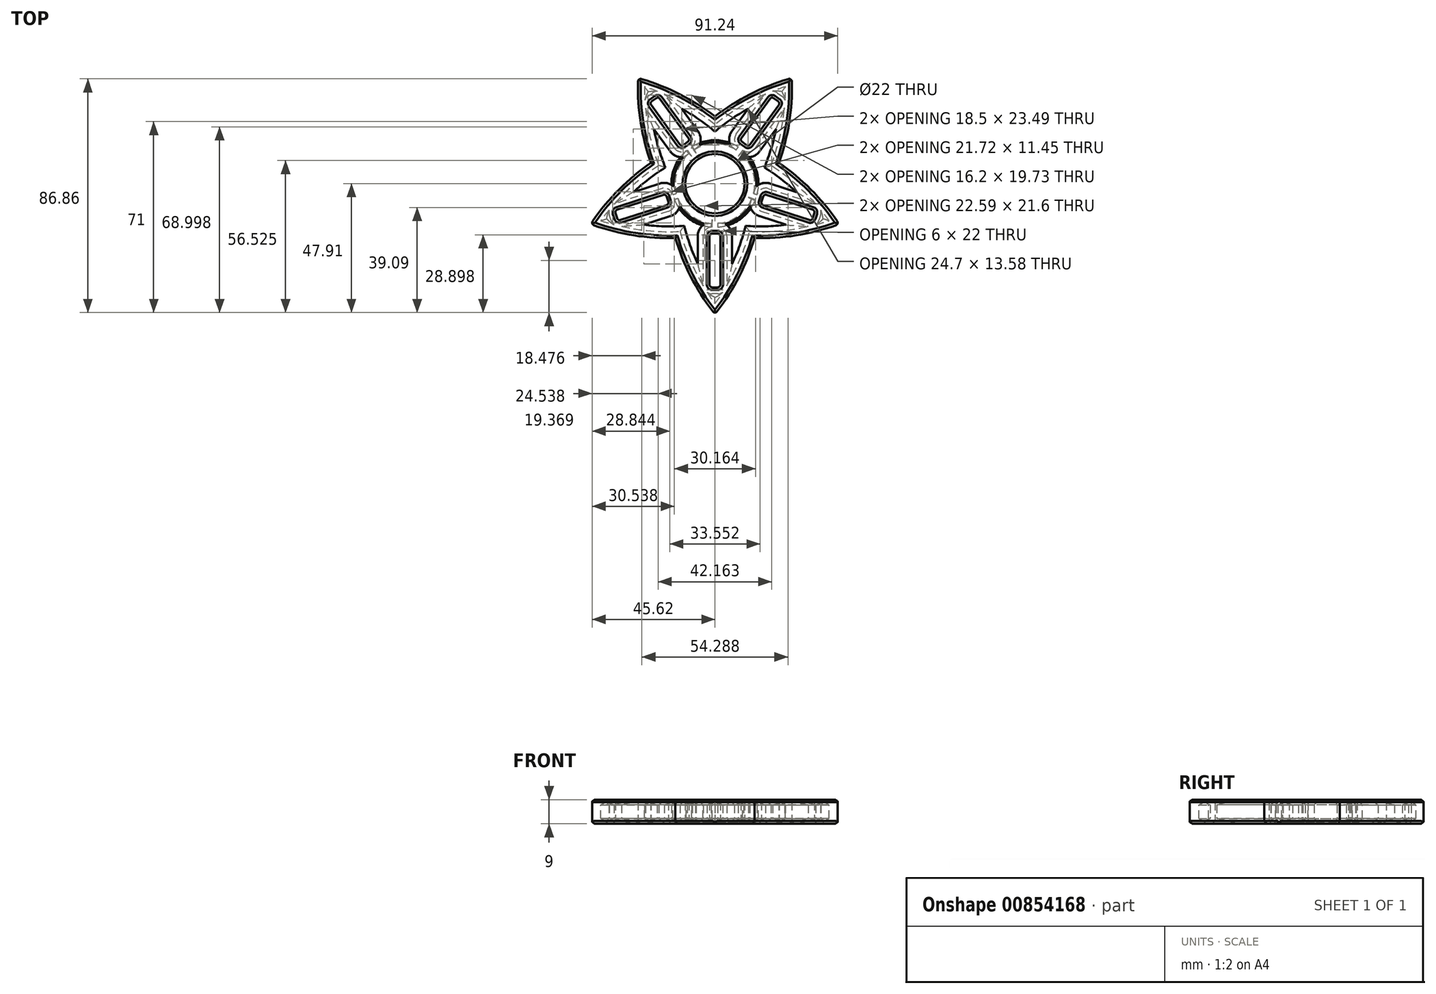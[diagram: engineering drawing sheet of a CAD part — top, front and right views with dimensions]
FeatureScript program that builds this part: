
annotation { "Feature Type Name" : "Feature", "Feature Type Description" : "" }
export const myFeature = defineFeature(function(context is Context, id is Id, definition is map)
    precondition{}
    {
        {
            var Q0;
            Q0=qCreatedBy(makeId("Top.planeOp"),FACE);
            var sketch = newSketch(context, id + "F0", { "sketchPlane" : qUnion([Q0])});
            skCircle(sketch, "E0", {"center": v(0, 0) * mm, "radius": 11 * mm});
            skCircle(sketch, "E1", {"center": v(0, 0) * mm, "radius": 15 * mm});
            skLineSegment(sketch, "E2.0", {"start": v(-10.9, 15) * mm, "end": v(10.9, 15) * mm});
            skLineSegment(sketch, "E2.1", {"start": v(10.9, 15) * mm, "end": v(17.63, -5.73) * mm});
            skLineSegment(sketch, "E2.2", {"start": v(17.63, -5.73) * mm, "end": v(0, -18.54) * mm});
            skLineSegment(sketch, "E2.3", {"start": v(0, -18.54) * mm, "end": v(-17.63, -5.73) * mm});
            skLineSegment(sketch, "E2.4", {"start": v(-17.63, -5.73) * mm, "end": v(-10.9, 15) * mm});
            skPoint(sketch, "E2.0.midPoint", {"position": v(0, 15) * mm});
            skLineSegment(sketch, "E3", {"start": v(-10.9, 15) * mm, "end": v(-28.53, 39.27) * mm});
            skLineSegment(sketch, "E4", {"start": v(-17.63, -5.73) * mm, "end": v(-46.17, -15) * mm});
            skLineSegment(sketch, "E5", {"start": v(0, -18.54) * mm, "end": v(0, -48.54) * mm});
            skLineSegment(sketch, "E6", {"start": v(17.63, -5.73) * mm, "end": v(46.17, -15) * mm});
            skLineSegment(sketch, "E7", {"start": v(10.9, 15) * mm, "end": v(28.53, 39.27) * mm});
            skLineSegment(sketch, "E8", {"start": v(14.27, 4.64) * mm, "end": v(23.78, 7.73) * mm});
            skLineSegment(sketch, "E9", {"start": v(0, 15) * mm, "end": v(0, 25) * mm});
            skLineSegment(sketch, "E10", {"start": v(-8.82, -12.14) * mm, "end": v(-14.7, -20.23) * mm});
            skLineSegment(sketch, "E11", {"start": v(8.82, -12.14) * mm, "end": v(14.7, -20.23) * mm});
            skLineSegment(sketch, "E12", {"start": v(-14.27, 4.64) * mm, "end": v(-23.78, 7.73) * mm});
            skArc(sketch, "E13", {"start": v(28.53, 39.27) * mm, "mid": v(7.11, 29.9) * mm, "end": v(-10.9, 15) * mm});
            skArc(sketch, "E14", {"start": v(-28.53, 39.27) * mm, "mid": v(-26.24, 16) * mm, "end": v(-17.63, -5.73) * mm});
            skArc(sketch, "E15", {"start": v(10.9, 15) * mm, "mid": v(-7.11, 29.9) * mm, "end": v(-28.53, 39.27) * mm});
            skArc(sketch, "E16", {"start": v(-10.9, 15) * mm, "mid": v(-30.64, 2.47) * mm, "end": v(-46.17, -15) * mm});
            skArc(sketch, "E17", {"start": v(-46.17, -15) * mm, "mid": v(-23.33, -20) * mm, "end": v(0, -18.54) * mm});
            skArc(sketch, "E18", {"start": v(-17.63, -5.73) * mm, "mid": v(-11.82, -28.37) * mm, "end": v(0, -48.54) * mm});
            skArc(sketch, "E19", {"start": v(0, -18.54) * mm, "mid": v(23.33, -20) * mm, "end": v(46.17, -15) * mm});
            skArc(sketch, "E20", {"start": v(0, -48.54) * mm, "mid": v(11.82, -28.37) * mm, "end": v(17.63, -5.73) * mm});
            skArc(sketch, "E21", {"start": v(17.63, -5.73) * mm, "mid": v(26.24, 16) * mm, "end": v(28.53, 39.27) * mm});
            skArc(sketch, "E22", {"start": v(46.17, -15) * mm, "mid": v(30.64, 2.47) * mm, "end": v(10.9, 15) * mm});
            skLineSegment(sketch, "E23", {"start": v(0, -18.54) * mm, "end": v(0, -33.54) * mm});
            skLineSegment(sketch, "E24.bottom", {"start": v(-1, -38.54) * mm, "end": v(1, -38.54) * mm});
            skLineSegment(sketch, "E24.top", {"start": v(-1, -18.54) * mm, "end": v(1, -18.54) * mm});
            skLineSegment(sketch, "E24.left", {"start": v(-2, -37.54) * mm, "end": v(-2, -19.54) * mm});
            skLineSegment(sketch, "E24.right", {"start": v(2, -37.54) * mm, "end": v(2, -19.54) * mm});
            skPoint(sketch, "E24.middle", {"position": v(0, -28.54) * mm});
            skPoint(sketch, "E25.visualSharp", {"position": v(-2, -18.54) * mm});
            skArc(sketch, "E25.filletArc", {"start": v(-1, -18.54) * mm, "mid": v(-1.7, -18.83) * mm, "end": v(-2, -19.54) * mm});
            skPoint(sketch, "E26.visualSharp", {"position": v(2, -18.54) * mm});
            skArc(sketch, "E26.filletArc", {"start": v(2, -19.54) * mm, "mid": v(1.7, -18.83) * mm, "end": v(1, -18.54) * mm});
            skPoint(sketch, "E27.visualSharp", {"position": v(-2, -38.54) * mm});
            skArc(sketch, "E27.filletArc", {"start": v(-2, -37.54) * mm, "mid": v(-1.7, -38.25) * mm, "end": v(-1, -38.54) * mm});
            skPoint(sketch, "E28.visualSharp", {"position": v(2, -38.54) * mm});
            skArc(sketch, "E28.filletArc", {"start": v(1, -38.54) * mm, "mid": v(1.7, -38.25) * mm, "end": v(2, -37.54) * mm});
            skLineSegment(sketch, "E29.1.0", {"start": v(35.09, -13.5) * mm, "end": v(17.97, -7.94) * mm});
            skPoint(sketch, "E29.1.1", {"position": v(18.25, -3.83) * mm});
            skPoint(sketch, "E29.1.2", {"position": v(36.04, -13.81) * mm});
            skLineSegment(sketch, "E29.1.3", {"start": v(36.32, -9.7) * mm, "end": v(19.2, -4.14) * mm});
            skPoint(sketch, "E29.1.4", {"position": v(17.02, -7.63) * mm});
            skPoint(sketch, "E29.1.5", {"position": v(37.27, -10) * mm});
            skLineSegment(sketch, "E29.1.6", {"start": v(17.63, -5.73) * mm, "end": v(31.9, -10.36) * mm});
            skArc(sketch, "E29.1.7", {"start": v(35.09, -13.5) * mm, "mid": v(35.85, -13.44) * mm, "end": v(36.35, -12.86) * mm});
            skArc(sketch, "E29.1.8", {"start": v(17.32, -6.68) * mm, "mid": v(17.38, -7.44) * mm, "end": v(17.97, -7.94) * mm});
            skArc(sketch, "E29.1.9", {"start": v(19.2, -4.14) * mm, "mid": v(18.44, -4.2) * mm, "end": v(17.94, -4.78) * mm});
            skArc(sketch, "E29.1.10", {"start": v(36.96, -10.96) * mm, "mid": v(36.9, -10.2) * mm, "end": v(36.32, -9.7) * mm});
            skLineSegment(sketch, "E29.1.11", {"start": v(36.35, -12.86) * mm, "end": v(36.96, -10.96) * mm});
            skLineSegment(sketch, "E29.1.12", {"start": v(17.32, -6.68) * mm, "end": v(17.94, -4.78) * mm});
            skPoint(sketch, "E29.1.13", {"position": v(27.14, -8.82) * mm});
            skLineSegment(sketch, "E29.2.0", {"start": v(23.68, 29.2) * mm, "end": v(13.1, 14.63) * mm});
            skPoint(sketch, "E29.2.1", {"position": v(9.28, 16.18) * mm});
            skPoint(sketch, "E29.2.2", {"position": v(24.27, 30) * mm});
            skLineSegment(sketch, "E29.2.3", {"start": v(20.45, 31.55) * mm, "end": v(9.87, 16.98) * mm});
            skPoint(sketch, "E29.2.4", {"position": v(12.52, 13.82) * mm});
            skPoint(sketch, "E29.2.5", {"position": v(21.04, 32.36) * mm});
            skLineSegment(sketch, "E29.2.6", {"start": v(10.9, 15) * mm, "end": v(19.71, 27.14) * mm});
            skArc(sketch, "E29.2.7", {"start": v(23.68, 29.2) * mm, "mid": v(23.86, 29.94) * mm, "end": v(23.46, 30.6) * mm});
            skArc(sketch, "E29.2.8", {"start": v(11.7, 14.41) * mm, "mid": v(12.45, 14.23) * mm, "end": v(13.1, 14.63) * mm});
            skArc(sketch, "E29.2.9", {"start": v(9.87, 16.98) * mm, "mid": v(9.69, 16.24) * mm, "end": v(10.09, 15.59) * mm});
            skArc(sketch, "E29.2.10", {"start": v(21.84, 31.77) * mm, "mid": v(21.1, 31.95) * mm, "end": v(20.45, 31.55) * mm});
            skLineSegment(sketch, "E29.2.11", {"start": v(23.46, 30.6) * mm, "end": v(21.84, 31.77) * mm});
            skLineSegment(sketch, "E29.2.12", {"start": v(11.7, 14.41) * mm, "end": v(10.09, 15.59) * mm});
            skPoint(sketch, "E29.2.13", {"position": v(16.78, 23.1) * mm});
            skLineSegment(sketch, "E29.3.0", {"start": v(-20.45, 31.55) * mm, "end": v(-9.87, 16.98) * mm});
            skPoint(sketch, "E29.3.1", {"position": v(-12.52, 13.82) * mm});
            skPoint(sketch, "E29.3.2", {"position": v(-21.04, 32.36) * mm});
            skLineSegment(sketch, "E29.3.3", {"start": v(-23.68, 29.2) * mm, "end": v(-13.1, 14.63) * mm});
            skPoint(sketch, "E29.3.4", {"position": v(-9.28, 16.18) * mm});
            skPoint(sketch, "E29.3.5", {"position": v(-24.27, 30) * mm});
            skLineSegment(sketch, "E29.3.6", {"start": v(-10.9, 15) * mm, "end": v(-19.71, 27.14) * mm});
            skArc(sketch, "E29.3.7", {"start": v(-20.45, 31.55) * mm, "mid": v(-21.1, 31.95) * mm, "end": v(-21.84, 31.77) * mm});
            skArc(sketch, "E29.3.8", {"start": v(-10.09, 15.59) * mm, "mid": v(-9.69, 16.24) * mm, "end": v(-9.87, 16.98) * mm});
            skArc(sketch, "E29.3.9", {"start": v(-13.1, 14.63) * mm, "mid": v(-12.45, 14.23) * mm, "end": v(-11.7, 14.41) * mm});
            skArc(sketch, "E29.3.10", {"start": v(-23.46, 30.6) * mm, "mid": v(-23.86, 29.94) * mm, "end": v(-23.68, 29.2) * mm});
            skLineSegment(sketch, "E29.3.11", {"start": v(-21.84, 31.77) * mm, "end": v(-23.46, 30.6) * mm});
            skLineSegment(sketch, "E29.3.12", {"start": v(-10.09, 15.59) * mm, "end": v(-11.7, 14.41) * mm});
            skPoint(sketch, "E29.3.13", {"position": v(-16.78, 23.1) * mm});
            skLineSegment(sketch, "E29.4.0", {"start": v(-36.32, -9.7) * mm, "end": v(-19.2, -4.14) * mm});
            skPoint(sketch, "E29.4.1", {"position": v(-17.02, -7.63) * mm});
            skPoint(sketch, "E29.4.2", {"position": v(-37.27, -10) * mm});
            skLineSegment(sketch, "E29.4.3", {"start": v(-35.09, -13.5) * mm, "end": v(-17.97, -7.94) * mm});
            skPoint(sketch, "E29.4.4", {"position": v(-18.25, -3.83) * mm});
            skPoint(sketch, "E29.4.5", {"position": v(-36.04, -13.81) * mm});
            skLineSegment(sketch, "E29.4.6", {"start": v(-17.63, -5.73) * mm, "end": v(-31.9, -10.36) * mm});
            skArc(sketch, "E29.4.7", {"start": v(-36.32, -9.7) * mm, "mid": v(-36.9, -10.2) * mm, "end": v(-36.96, -10.96) * mm});
            skArc(sketch, "E29.4.8", {"start": v(-17.94, -4.78) * mm, "mid": v(-18.44, -4.2) * mm, "end": v(-19.2, -4.14) * mm});
            skArc(sketch, "E29.4.9", {"start": v(-17.97, -7.94) * mm, "mid": v(-17.38, -7.44) * mm, "end": v(-17.32, -6.68) * mm});
            skArc(sketch, "E29.4.10", {"start": v(-36.35, -12.86) * mm, "mid": v(-35.85, -13.44) * mm, "end": v(-35.09, -13.5) * mm});
            skLineSegment(sketch, "E29.4.11", {"start": v(-36.96, -10.96) * mm, "end": v(-36.35, -12.86) * mm});
            skLineSegment(sketch, "E29.4.12", {"start": v(-17.94, -4.78) * mm, "end": v(-17.32, -6.68) * mm});
            skPoint(sketch, "E29.4.13", {"position": v(-27.14, -8.82) * mm});
            skSolve(sketch);
        }
        {
            var Q0;
            {var subQ3=sQuery(id+"F0.wireOp",EDGE,"E9");Q0=makeQuery(id+"F0.imprint","IMPRINT",FACE,{"disambiguationData":[TD([[makeQuery(id+"F0.imprint","IMPRINT",EDGE,{"derivedFrom":subQ3}),1.0]])]});}
            var Q1;
            {var subQ3=sQuery(id+"F0.wireOp",EDGE,"E9");Q1=makeQuery(id+"F0.imprint","IMPRINT",FACE,{"disambiguationData":[TD([[makeQuery(id+"F0.imprint","IMPRINT",EDGE,{"derivedFrom":subQ3}),-1.0]])]});}
            var Q2;
            {var subQ3=sQuery(id+"F0.wireOp",EDGE,"E8");Q2=makeQuery(id+"F0.imprint","IMPRINT",FACE,{"disambiguationData":[TD([[makeQuery(id+"F0.imprint","IMPRINT",EDGE,{"derivedFrom":subQ3}),1.0]])]});}
            var Q3;
            {var subQ3=sQuery(id+"F0.wireOp",EDGE,"E8");Q3=makeQuery(id+"F0.imprint","IMPRINT",FACE,{"disambiguationData":[TD([[makeQuery(id+"F0.imprint","IMPRINT",EDGE,{"derivedFrom":subQ3}),-1.0]])]});}
            var Q4;
            {var subQ3=sQuery(id+"F0.wireOp",EDGE,"E11");Q4=makeQuery(id+"F0.imprint","IMPRINT",FACE,{"disambiguationData":[TD([[makeQuery(id+"F0.imprint","IMPRINT",EDGE,{"derivedFrom":subQ3}),1.0]])]});}
            var Q5;
            {var subQ3=sQuery(id+"F0.wireOp",EDGE,"E11");Q5=makeQuery(id+"F0.imprint","IMPRINT",FACE,{"disambiguationData":[TD([[makeQuery(id+"F0.imprint","IMPRINT",EDGE,{"derivedFrom":subQ3}),-1.0]])]});}
            var Q6;
            {var subQ3=sQuery(id+"F0.wireOp",EDGE,"E10");Q6=makeQuery(id+"F0.imprint","IMPRINT",FACE,{"disambiguationData":[TD([[makeQuery(id+"F0.imprint","IMPRINT",EDGE,{"derivedFrom":subQ3}),1.0]])]});}
            var Q7;
            {var subQ3=sQuery(id+"F0.wireOp",EDGE,"E10");Q7=makeQuery(id+"F0.imprint","IMPRINT",FACE,{"disambiguationData":[TD([[makeQuery(id+"F0.imprint","IMPRINT",EDGE,{"derivedFrom":subQ3}),-1.0]])]});}
            var Q8;
            {var subQ3=sQuery(id+"F0.wireOp",EDGE,"E12");Q8=makeQuery(id+"F0.imprint","IMPRINT",FACE,{"disambiguationData":[TD([[makeQuery(id+"F0.imprint","IMPRINT",EDGE,{"derivedFrom":subQ3}),1.0]])]});}
            var Q9;
            {var subQ3=sQuery(id+"F0.wireOp",EDGE,"E12");Q9=makeQuery(id+"F0.imprint","IMPRINT",FACE,{"disambiguationData":[TD([[makeQuery(id+"F0.imprint","IMPRINT",EDGE,{"derivedFrom":subQ3}),-1.0]])]});}
            var Q10;
            Q10=makeQuery(id+"F0.imprint","IMPRINT",FACE,{"disambiguationData":[TD([[makeQuery(id+"F0.imprint","IMPRINT",EDGE,{"derivedFrom":sQuery(id+"F0.wireOp",EDGE,"03f61230-8e6a-4787-a5c0-0c1afcc67b7a.3.3")}),-1.0]])]});
            var Q11;
            Q11=makeQuery(id+"F0.imprint","IMPRINT",FACE,{"disambiguationData":[TD([[makeQuery(id+"F0.imprint","IMPRINT",EDGE,{"derivedFrom":sQuery(id+"F0.wireOp",EDGE,"03f61230-8e6a-4787-a5c0-0c1afcc67b7a.4.1")}),1.0]])]});
            var Q12;
            Q12=makeQuery(id+"F0.imprint","IMPRINT",FACE,{"disambiguationData":[TD([[makeQuery(id+"F0.imprint","IMPRINT",EDGE,{"derivedFrom":sQuery(id+"F0.wireOp",EDGE,"03f61230-8e6a-4787-a5c0-0c1afcc67b7a.4.3")}),-1.0]])]});
            var Q13;
            Q13=makeQuery(id+"F0.imprint","IMPRINT",FACE,{"disambiguationData":[TD([[makeQuery(id+"F0.imprint","IMPRINT",EDGE,{"derivedFrom":sQuery(id+"F0.wireOp",EDGE,"E24.left")}),1.0]])]});
            var Q14;
            Q14=makeQuery(id+"F0.imprint","IMPRINT",FACE,{"disambiguationData":[TD([[makeQuery(id+"F0.imprint","IMPRINT",EDGE,{"derivedFrom":sQuery(id+"F0.wireOp",EDGE,"E24.right")}),-1.0]])]});
            var Q15;
            Q15=makeQuery(id+"F0.imprint","IMPRINT",FACE,{"disambiguationData":[TD([[makeQuery(id+"F0.imprint","IMPRINT",EDGE,{"derivedFrom":sQuery(id+"F0.wireOp",EDGE,"03f61230-8e6a-4787-a5c0-0c1afcc67b7a.1.1")}),1.0]])]});
            var Q16;
            Q16=makeQuery(id+"F0.imprint","IMPRINT",FACE,{"disambiguationData":[TD([[makeQuery(id+"F0.imprint","IMPRINT",EDGE,{"derivedFrom":sQuery(id+"F0.wireOp",EDGE,"03f61230-8e6a-4787-a5c0-0c1afcc67b7a.1.3")}),-1.0]])]});
            var Q17;
            Q17=makeQuery(id+"F0.imprint","IMPRINT",FACE,{"disambiguationData":[TD([[makeQuery(id+"F0.imprint","IMPRINT",EDGE,{"derivedFrom":sQuery(id+"F0.wireOp",EDGE,"03f61230-8e6a-4787-a5c0-0c1afcc67b7a.2.3")}),-1.0]])]});
            var Q18;
            Q18=makeQuery(id+"F0.imprint","IMPRINT",FACE,{"disambiguationData":[TD([[makeQuery(id+"F0.imprint","IMPRINT",EDGE,{"derivedFrom":sQuery(id+"F0.wireOp",EDGE,"03f61230-8e6a-4787-a5c0-0c1afcc67b7a.2.1")}),1.0]])]});
            var Q19;
            Q19=makeQuery(id+"F0.imprint","IMPRINT",FACE,{"disambiguationData":[TD([[makeQuery(id+"F0.imprint","IMPRINT",EDGE,{"derivedFrom":sQuery(id+"F0.wireOp",EDGE,"03f61230-8e6a-4787-a5c0-0c1afcc67b7a.3.1")}),1.0]])]});
            var Q20;
            {var subQ0=sQuery(id+"F0.wireOp",EDGE,"E2.0");var subQ1=sQuery(id+"F0.wireOp",EDGE,"E1");var subQ2=makeQuery(id+"F0.imprint","INTERSECT",VERTEX,{"derivedFrom":[subQ1,subQ0,sQuery(id+"F0.wireOp",EDGE,"E9")]});Q20=makeQuery(id+"F0.imprint","IMPRINT",FACE,{"disambiguationData":[TD([[makeQuery(id+"F0.imprint","IMPRINT",EDGE,{"disambiguationData":[TD([[subQ2,-1.0]])],"derivedFrom":subQ1}),-1.0]])]});}
            var Q21;
            {var subQ0=sQuery(id+"F0.wireOp",EDGE,"E2.3");var subQ1=sQuery(id+"F0.wireOp",EDGE,"E1");var subQ2=makeQuery(id+"F0.imprint","INTERSECT",VERTEX,{"derivedFrom":[subQ1,subQ0,sQuery(id+"F0.wireOp",EDGE,"E10")]});Q21=makeQuery(id+"F0.imprint","IMPRINT",FACE,{"disambiguationData":[TD([[makeQuery(id+"F0.imprint","IMPRINT",EDGE,{"disambiguationData":[TD([[subQ2,1.0]])],"derivedFrom":subQ1}),-1.0]])]});}
            var Q22;
            {var subQ0=sQuery(id+"F0.wireOp",EDGE,"E2.3");var subQ1=sQuery(id+"F0.wireOp",EDGE,"E1");var subQ2=makeQuery(id+"F0.imprint","INTERSECT",VERTEX,{"derivedFrom":[subQ1,subQ0,sQuery(id+"F0.wireOp",EDGE,"E10")]});Q22=makeQuery(id+"F0.imprint","IMPRINT",FACE,{"disambiguationData":[TD([[makeQuery(id+"F0.imprint","IMPRINT",EDGE,{"disambiguationData":[TD([[subQ2,-1.0]])],"derivedFrom":subQ1}),-1.0]])]});}
            var Q23;
            {var subQ0=sQuery(id+"F0.wireOp",EDGE,"E2.1");var subQ1=sQuery(id+"F0.wireOp",EDGE,"E1");var subQ2=makeQuery(id+"F0.imprint","INTERSECT",VERTEX,{"derivedFrom":[subQ1,subQ0,sQuery(id+"F0.wireOp",EDGE,"E8")]});Q23=makeQuery(id+"F0.imprint","IMPRINT",FACE,{"disambiguationData":[TD([[makeQuery(id+"F0.imprint","IMPRINT",EDGE,{"disambiguationData":[TD([[subQ2,1.0]])],"derivedFrom":subQ1}),-1.0]])]});}
            var Q24;
            {var subQ0=sQuery(id+"F0.wireOp",EDGE,"E2.1");var subQ1=sQuery(id+"F0.wireOp",EDGE,"E1");var subQ2=makeQuery(id+"F0.imprint","INTERSECT",VERTEX,{"derivedFrom":[subQ1,subQ0,sQuery(id+"F0.wireOp",EDGE,"E8")]});Q24=makeQuery(id+"F0.imprint","IMPRINT",FACE,{"disambiguationData":[TD([[makeQuery(id+"F0.imprint","IMPRINT",EDGE,{"disambiguationData":[TD([[subQ2,-1.0]])],"derivedFrom":subQ1}),-1.0]])]});}
            var Q25;
            Q25=makeQuery(id+"F0.imprint","IMPRINT",FACE,{"disambiguationData":[TD([[makeQuery(id+"F0.imprint","IMPRINT",EDGE,{"derivedFrom":sQuery(id+"F0.wireOp",EDGE,"E0")}),-1.0]])]});
            var Q26;
            {var subQ0=sQuery(id+"F0.wireOp",EDGE,"E29.4.0");Q26=makeQuery(id+"F0.imprint","IMPRINT",FACE,{"disambiguationData":[TD([[makeQuery(id+"F0.imprint","IMPRINT",EDGE,{"derivedFrom":subQ0}),1.0]])]});}
            var Q27;
            {var subQ7=sQuery(id+"F0.wireOp",EDGE,"E29.4.3");Q27=makeQuery(id+"F0.imprint","IMPRINT",FACE,{"disambiguationData":[TD([[makeQuery(id+"F0.imprint","IMPRINT",EDGE,{"derivedFrom":subQ7}),-1.0]])]});}
            var Q28;
            {var subQ0=sQuery(id+"F0.wireOp",EDGE,"E29.3.3");Q28=makeQuery(id+"F0.imprint","IMPRINT",FACE,{"disambiguationData":[TD([[makeQuery(id+"F0.imprint","IMPRINT",EDGE,{"derivedFrom":subQ0}),-1.0]])]});}
            var Q29;
            {var subQ0=sQuery(id+"F0.wireOp",EDGE,"E29.3.0");Q29=makeQuery(id+"F0.imprint","IMPRINT",FACE,{"disambiguationData":[TD([[makeQuery(id+"F0.imprint","IMPRINT",EDGE,{"derivedFrom":subQ0}),1.0]])]});}
            var Q30;
            {var subQ0=sQuery(id+"F0.wireOp",EDGE,"E29.2.3");Q30=makeQuery(id+"F0.imprint","IMPRINT",FACE,{"disambiguationData":[TD([[makeQuery(id+"F0.imprint","IMPRINT",EDGE,{"derivedFrom":subQ0}),-1.0]])]});}
            var Q31;
            {var subQ5=sQuery(id+"F0.wireOp",EDGE,"E29.2.0");Q31=makeQuery(id+"F0.imprint","IMPRINT",FACE,{"disambiguationData":[TD([[makeQuery(id+"F0.imprint","IMPRINT",EDGE,{"derivedFrom":subQ5}),1.0]])]});}
            var Q32;
            {var subQ0=sQuery(id+"F0.wireOp",EDGE,"E29.1.3");Q32=makeQuery(id+"F0.imprint","IMPRINT",FACE,{"disambiguationData":[TD([[makeQuery(id+"F0.imprint","IMPRINT",EDGE,{"derivedFrom":subQ0}),-1.0]])]});}
            var Q33;
            {var subQ0=sQuery(id+"F0.wireOp",EDGE,"E29.1.0");Q33=makeQuery(id+"F0.imprint","IMPRINT",FACE,{"disambiguationData":[TD([[makeQuery(id+"F0.imprint","IMPRINT",EDGE,{"derivedFrom":subQ0}),1.0]])]});}
            extrude(context, id + "F1", {"entities" : qUnion([Q0, Q1, Q2, Q3, Q4, Q5, Q6, Q7, Q8, Q9, Q10, Q11, Q12, Q13, Q14, Q15, Q16, Q17, Q18, Q19, Q20, Q21, Q22, Q23, Q24, Q25, Q26, Q27, Q28, Q29, Q30, Q31, Q32, Q33]), "depth" : 9 * mm, "offsetDistance" : 25 * mm});
        }
        {
            var Q0;
            Q0=makeQuery(id+"F1.opExtrude","CAP_EDGE",EDGE,{"disambiguationData":[OSD([sQuery(id+"F0.wireOp",EDGE,"E20")])],"isStart":false});
            var Q1;
            Q1=makeQuery(id+"F1.opExtrude","CAP_EDGE",EDGE,{"disambiguationData":[OSD([sQuery(id+"F0.wireOp",EDGE,"E19")])],"isStart":false});
            var Q2;
            Q2=makeQuery(id+"F1.opExtrude","CAP_EDGE",EDGE,{"disambiguationData":[OSD([sQuery(id+"F0.wireOp",EDGE,"E22")])],"isStart":false});
            var Q3;
            Q3=makeQuery(id+"F1.opExtrude","CAP_EDGE",EDGE,{"disambiguationData":[OSD([sQuery(id+"F0.wireOp",EDGE,"E21")])],"isStart":false});
            var Q4;
            Q4=makeQuery(id+"F1.opExtrude","CAP_EDGE",EDGE,{"disambiguationData":[OSD([sQuery(id+"F0.wireOp",EDGE,"E13")])],"isStart":false});
            var Q5;
            Q5=makeQuery(id+"F1.opExtrude","CAP_EDGE",EDGE,{"disambiguationData":[OSD([sQuery(id+"F0.wireOp",EDGE,"E15")])],"isStart":false});
            var Q6;
            Q6=makeQuery(id+"F1.opExtrude","CAP_EDGE",EDGE,{"disambiguationData":[OSD([sQuery(id+"F0.wireOp",EDGE,"E14")])],"isStart":false});
            var Q7;
            Q7=makeQuery(id+"F1.opExtrude","CAP_EDGE",EDGE,{"disambiguationData":[OSD([sQuery(id+"F0.wireOp",EDGE,"E16")])],"isStart":false});
            var Q8;
            Q8=makeQuery(id+"F1.opExtrude","CAP_EDGE",EDGE,{"disambiguationData":[OSD([sQuery(id+"F0.wireOp",EDGE,"E17")])],"isStart":false});
            var Q9;
            Q9=makeQuery(id+"F1.opExtrude","CAP_EDGE",EDGE,{"disambiguationData":[OSD([sQuery(id+"F0.wireOp",EDGE,"E17")])],"isStart":true});
            var Q10;
            Q10=makeQuery(id+"F1.opExtrude","CAP_EDGE",EDGE,{"disambiguationData":[OSD([sQuery(id+"F0.wireOp",EDGE,"E20")])],"isStart":true});
            var Q11;
            Q11=makeQuery(id+"F1.opExtrude","CAP_EDGE",EDGE,{"disambiguationData":[OSD([sQuery(id+"F0.wireOp",EDGE,"E19")])],"isStart":true});
            var Q12;
            Q12=makeQuery(id+"F1.opExtrude","CAP_EDGE",EDGE,{"disambiguationData":[OSD([sQuery(id+"F0.wireOp",EDGE,"E21")])],"isStart":true});
            var Q13;
            Q13=makeQuery(id+"F1.opExtrude","CAP_EDGE",EDGE,{"disambiguationData":[OSD([sQuery(id+"F0.wireOp",EDGE,"E18")])],"isStart":true});
            var Q14;
            Q14=makeQuery(id+"F1.opExtrude","CAP_EDGE",EDGE,{"disambiguationData":[OSD([sQuery(id+"F0.wireOp",EDGE,"E16")])],"isStart":true});
            var Q15;
            Q15=makeQuery(id+"F1.opExtrude","CAP_EDGE",EDGE,{"disambiguationData":[OSD([sQuery(id+"F0.wireOp",EDGE,"E14")])],"isStart":true});
            var Q16;
            Q16=makeQuery(id+"F1.opExtrude","CAP_EDGE",EDGE,{"disambiguationData":[OSD([sQuery(id+"F0.wireOp",EDGE,"E15")])],"isStart":true});
            var Q17;
            Q17=makeQuery(id+"F1.opExtrude","CAP_EDGE",EDGE,{"disambiguationData":[OSD([sQuery(id+"F0.wireOp",EDGE,"E13")])],"isStart":true});
            var Q18;
            Q18=makeQuery(id+"F1.opExtrude","CAP_EDGE",EDGE,{"disambiguationData":[OSD([sQuery(id+"F0.wireOp",EDGE,"E22")])],"isStart":true});
            var Q19;
            Q19=makeQuery(id+"F1.opExtrude","CAP_EDGE",EDGE,{"disambiguationData":[OSD([sQuery(id+"F0.wireOp",EDGE,"E18")])],"isStart":false});
            chamfer(context, id + "F2", {"entities" : qUnion([Q0, Q1, Q2, Q3, Q4, Q5, Q6, Q7, Q8, Q9, Q10, Q11, Q12, Q13, Q14, Q15, Q16, Q17, Q18, Q19]), "width" : 1 * mm, "tangentPropagation" : true});
        }
        {
            var Q0;
            Q0=makeQuery(id+"F1.opExtrude","SWEPT_EDGE",EDGE,{"disambiguationData":[OSD([sQuery(id+"F0.wireOp",EDGE,"E5"),sQuery(id+"F0.wireOp",EDGE,"E18"),sQuery(id+"F0.wireOp",EDGE,"E20")])]});
            var Q1;
            Q1=makeQuery(id+"F1.opExtrude","SWEPT_EDGE",EDGE,{"disambiguationData":[OSD([sQuery(id+"F0.wireOp",EDGE,"E6"),sQuery(id+"F0.wireOp",EDGE,"E19"),sQuery(id+"F0.wireOp",EDGE,"E22")])]});
            var Q2;
            Q2=makeQuery(id+"F1.opExtrude","SWEPT_EDGE",EDGE,{"disambiguationData":[OSD([sQuery(id+"F0.wireOp",EDGE,"E7"),sQuery(id+"F0.wireOp",EDGE,"E13"),sQuery(id+"F0.wireOp",EDGE,"E21")])]});
            var Q3;
            Q3=makeQuery(id+"F1.opExtrude","SWEPT_EDGE",EDGE,{"disambiguationData":[OSD([sQuery(id+"F0.wireOp",EDGE,"E3"),sQuery(id+"F0.wireOp",EDGE,"E14"),sQuery(id+"F0.wireOp",EDGE,"E15")])]});
            var Q4;
            Q4=makeQuery(id+"F1.opExtrude","SWEPT_EDGE",EDGE,{"disambiguationData":[OSD([sQuery(id+"F0.wireOp",EDGE,"E4"),sQuery(id+"F0.wireOp",EDGE,"E16"),sQuery(id+"F0.wireOp",EDGE,"E17")])]});
            fillet(context, id + "F3", {"entities" : qUnion([Q0, Q1, Q2, Q3, Q4]), "radius" : 1 * mm, "tangentPropagation" : true, "allowEdgeOverflow" : false});
        }
        {
            var Q0;
            Q0=makeQuery(id+"F1.opExtrude","CAP_EDGE",EDGE,{"disambiguationData":[OSD([sQuery(id+"F0.wireOp",EDGE,"E24.left")])],"isStart":false});
            var Q1;
            Q1=makeQuery(id+"F1.opExtrude","CAP_EDGE",EDGE,{"disambiguationData":[OSD([sQuery(id+"F0.wireOp",EDGE,"E29.4.0")])],"isStart":false});
            var Q2;
            Q2=makeQuery(id+"F1.opExtrude","CAP_EDGE",EDGE,{"disambiguationData":[OSD([sQuery(id+"F0.wireOp",EDGE,"E29.3.0")])],"isStart":false});
            var Q3;
            Q3=makeQuery(id+"F1.opExtrude","CAP_EDGE",EDGE,{"disambiguationData":[OSD([sQuery(id+"F0.wireOp",EDGE,"E29.2.3")])],"isStart":false});
            var Q4;
            Q4=makeQuery(id+"F1.opExtrude","CAP_EDGE",EDGE,{"disambiguationData":[OSD([sQuery(id+"F0.wireOp",EDGE,"E29.1.3")])],"isStart":false});
            var Q5;
            Q5=makeQuery(id+"F1.opExtrude","CAP_EDGE",EDGE,{"disambiguationData":[OSD([sQuery(id+"F0.wireOp",EDGE,"E29.4.0")])],"isStart":true});
            var Q6;
            Q6=makeQuery(id+"F1.opExtrude","CAP_EDGE",EDGE,{"disambiguationData":[OSD([sQuery(id+"F0.wireOp",EDGE,"E24.top")])],"isStart":true});
            var Q7;
            Q7=makeQuery(id+"F1.opExtrude","CAP_EDGE",EDGE,{"disambiguationData":[OSD([sQuery(id+"F0.wireOp",EDGE,"E29.1.3")])],"isStart":true});
            var Q8;
            Q8=makeQuery(id+"F1.opExtrude","CAP_EDGE",EDGE,{"disambiguationData":[OSD([sQuery(id+"F0.wireOp",EDGE,"E29.2.3")])],"isStart":true});
            var Q9;
            Q9=makeQuery(id+"F1.opExtrude","CAP_EDGE",EDGE,{"disambiguationData":[OSD([sQuery(id+"F0.wireOp",EDGE,"E29.3.0")])],"isStart":true});
            chamfer(context, id + "F4", {"entities" : qUnion([Q0, Q1, Q2, Q3, Q4, Q5, Q6, Q7, Q8, Q9]), "width" : 1 * mm, "tangentPropagation" : true});
        }
        {
            var Q0;
            Q0=makeQuery(id+"F1.opExtrude","CAP_EDGE",EDGE,{"disambiguationData":[OSD([sQuery(id+"F0.wireOp",EDGE,"E0")])],"isStart":false});
            var Q1;
            Q1=makeQuery(id+"F1.opExtrude","CAP_EDGE",EDGE,{"disambiguationData":[OSD([sQuery(id+"F0.wireOp",EDGE,"E0")])],"isStart":true});
            chamfer(context, id + "F5", {"entities" : qUnion([Q0, Q1]), "width" : 1 * mm, "tangentPropagation" : true});
        }
        {
            var Q0;
            Q0=makeQuery(id+"F1.opExtrude","CAP_FACE",FACE,{"disambiguationData":[OSD([sQuery(id+"F0.wireOp",EDGE,"E0"),sQuery(id+"F0.wireOp",EDGE,"E13"),sQuery(id+"F0.wireOp",EDGE,"E14"),sQuery(id+"F0.wireOp",EDGE,"E15"),sQuery(id+"F0.wireOp",EDGE,"E16"),sQuery(id+"F0.wireOp",EDGE,"E17"),sQuery(id+"F0.wireOp",EDGE,"E18"),sQuery(id+"F0.wireOp",EDGE,"E19"),sQuery(id+"F0.wireOp",EDGE,"E20"),sQuery(id+"F0.wireOp",EDGE,"E21"),sQuery(id+"F0.wireOp",EDGE,"E22"),sQuery(id+"F0.wireOp",EDGE,"E24.bottom"),sQuery(id+"F0.wireOp",EDGE,"E24.top"),sQuery(id+"F0.wireOp",EDGE,"E24.left"),sQuery(id+"F0.wireOp",EDGE,"E24.right"),sQuery(id+"F0.wireOp",EDGE,"E25.filletArc"),sQuery(id+"F0.wireOp",EDGE,"E26.filletArc"),sQuery(id+"F0.wireOp",EDGE,"E27.filletArc"),sQuery(id+"F0.wireOp",EDGE,"E28.filletArc"),sQuery(id+"F0.wireOp",EDGE,"E29.1.0"),sQuery(id+"F0.wireOp",EDGE,"E29.1.3"),sQuery(id+"F0.wireOp",EDGE,"E29.1.7"),sQuery(id+"F0.wireOp",EDGE,"E29.1.8"),sQuery(id+"F0.wireOp",EDGE,"E29.1.9"),sQuery(id+"F0.wireOp",EDGE,"E29.1.10"),sQuery(id+"F0.wireOp",EDGE,"E29.1.11"),sQuery(id+"F0.wireOp",EDGE,"E29.1.12"),sQuery(id+"F0.wireOp",EDGE,"E29.2.0"),sQuery(id+"F0.wireOp",EDGE,"E29.2.3"),sQuery(id+"F0.wireOp",EDGE,"E29.2.7"),sQuery(id+"F0.wireOp",EDGE,"E29.2.8"),sQuery(id+"F0.wireOp",EDGE,"E29.2.9"),sQuery(id+"F0.wireOp",EDGE,"E29.2.10"),sQuery(id+"F0.wireOp",EDGE,"E29.2.11"),sQuery(id+"F0.wireOp",EDGE,"E29.2.12"),sQuery(id+"F0.wireOp",EDGE,"E29.3.0"),sQuery(id+"F0.wireOp",EDGE,"E29.3.3"),sQuery(id+"F0.wireOp",EDGE,"E29.3.7"),sQuery(id+"F0.wireOp",EDGE,"E29.3.8"),sQuery(id+"F0.wireOp",EDGE,"E29.3.9"),sQuery(id+"F0.wireOp",EDGE,"E29.3.10"),sQuery(id+"F0.wireOp",EDGE,"E29.3.11"),sQuery(id+"F0.wireOp",EDGE,"E29.3.12"),sQuery(id+"F0.wireOp",EDGE,"E29.4.0"),sQuery(id+"F0.wireOp",EDGE,"E29.4.3"),sQuery(id+"F0.wireOp",EDGE,"E29.4.7"),sQuery(id+"F0.wireOp",EDGE,"E29.4.8"),sQuery(id+"F0.wireOp",EDGE,"E29.4.9"),sQuery(id+"F0.wireOp",EDGE,"E29.4.10"),sQuery(id+"F0.wireOp",EDGE,"E29.4.11"),sQuery(id+"F0.wireOp",EDGE,"E29.4.12")])],"isStart":false});
            var Q1;
            Q1=makeQuery(id+"F1.opExtrude","CAP_FACE",FACE,{"disambiguationData":[OSD([sQuery(id+"F0.wireOp",EDGE,"E0"),sQuery(id+"F0.wireOp",EDGE,"E13"),sQuery(id+"F0.wireOp",EDGE,"E14"),sQuery(id+"F0.wireOp",EDGE,"E15"),sQuery(id+"F0.wireOp",EDGE,"E16"),sQuery(id+"F0.wireOp",EDGE,"E17"),sQuery(id+"F0.wireOp",EDGE,"E18"),sQuery(id+"F0.wireOp",EDGE,"E19"),sQuery(id+"F0.wireOp",EDGE,"E20"),sQuery(id+"F0.wireOp",EDGE,"E21"),sQuery(id+"F0.wireOp",EDGE,"E22"),sQuery(id+"F0.wireOp",EDGE,"E24.bottom"),sQuery(id+"F0.wireOp",EDGE,"E24.top"),sQuery(id+"F0.wireOp",EDGE,"E24.left"),sQuery(id+"F0.wireOp",EDGE,"E24.right"),sQuery(id+"F0.wireOp",EDGE,"E25.filletArc"),sQuery(id+"F0.wireOp",EDGE,"E26.filletArc"),sQuery(id+"F0.wireOp",EDGE,"E27.filletArc"),sQuery(id+"F0.wireOp",EDGE,"E28.filletArc"),sQuery(id+"F0.wireOp",EDGE,"E29.1.0"),sQuery(id+"F0.wireOp",EDGE,"E29.1.3"),sQuery(id+"F0.wireOp",EDGE,"E29.1.7"),sQuery(id+"F0.wireOp",EDGE,"E29.1.8"),sQuery(id+"F0.wireOp",EDGE,"E29.1.9"),sQuery(id+"F0.wireOp",EDGE,"E29.1.10"),sQuery(id+"F0.wireOp",EDGE,"E29.1.11"),sQuery(id+"F0.wireOp",EDGE,"E29.1.12"),sQuery(id+"F0.wireOp",EDGE,"E29.2.0"),sQuery(id+"F0.wireOp",EDGE,"E29.2.3"),sQuery(id+"F0.wireOp",EDGE,"E29.2.7"),sQuery(id+"F0.wireOp",EDGE,"E29.2.8"),sQuery(id+"F0.wireOp",EDGE,"E29.2.9"),sQuery(id+"F0.wireOp",EDGE,"E29.2.10"),sQuery(id+"F0.wireOp",EDGE,"E29.2.11"),sQuery(id+"F0.wireOp",EDGE,"E29.2.12"),sQuery(id+"F0.wireOp",EDGE,"E29.3.0"),sQuery(id+"F0.wireOp",EDGE,"E29.3.3"),sQuery(id+"F0.wireOp",EDGE,"E29.3.7"),sQuery(id+"F0.wireOp",EDGE,"E29.3.8"),sQuery(id+"F0.wireOp",EDGE,"E29.3.9"),sQuery(id+"F0.wireOp",EDGE,"E29.3.10"),sQuery(id+"F0.wireOp",EDGE,"E29.3.11"),sQuery(id+"F0.wireOp",EDGE,"E29.3.12"),sQuery(id+"F0.wireOp",EDGE,"E29.4.0"),sQuery(id+"F0.wireOp",EDGE,"E29.4.3"),sQuery(id+"F0.wireOp",EDGE,"E29.4.7"),sQuery(id+"F0.wireOp",EDGE,"E29.4.8"),sQuery(id+"F0.wireOp",EDGE,"E29.4.9"),sQuery(id+"F0.wireOp",EDGE,"E29.4.10"),sQuery(id+"F0.wireOp",EDGE,"E29.4.11"),sQuery(id+"F0.wireOp",EDGE,"E29.4.12")])],"isStart":true});
            shell(context, id + "F6", {"entities" : qUnion([Q0, Q1]), "thickness" : 2.4 * mm});
        }
        {
            var Q0;
            {var subQ0=sQuery(id+"F0.wireOp",EDGE,"E29.4.12");Q0=makeQuery(id+"F6.opShell","OFFSET_FACE",FACE,{"disambiguationData":[OSD([subQ0]),TDD([makeQuery(id+"F1.opExtrude","SWEPT_FACE",FACE,{"disambiguationData":[OSD([subQ0])]})])]});}
            var Q1;
            {var subQ0=sQuery(id+"F0.wireOp",EDGE,"E29.4.12");Q1=makeQuery(id+"F6.opShell","OFFSET_FACE",FACE,{"disambiguationData":[OSD([subQ0]),TDD([makeQuery(id+"F4.opChamfer","BLEND_FACE",FACE,{"disambiguationData":[OSD([subQ0]),TDD([makeQuery(id+"F1.opExtrude","CAP_EDGE",EDGE,{"disambiguationData":[OSD([subQ0])],"isStart":true})])]})])]});}
            var Q2;
            {var subQ0=sQuery(id+"F0.wireOp",EDGE,"E29.4.12");Q2=makeQuery(id+"F6.opShell","OFFSET_FACE",FACE,{"disambiguationData":[OSD([subQ0]),TDD([makeQuery(id+"F4.opChamfer","BLEND_FACE",FACE,{"disambiguationData":[OSD([subQ0]),TDD([makeQuery(id+"F1.opExtrude","CAP_EDGE",EDGE,{"disambiguationData":[OSD([subQ0])],"isStart":false})])]})])]});}
            extrude(context, id + "F7", {"entities" : qUnion([Q0, Q1, Q2]), "operationType" : NewBodyOperationType.ADD, "endBound" : BoundingType.UP_TO_NEXT, "depth" : 3 * mm, "offsetDistance" : 25 * mm});
        }
        {
            var Q0;
            {var subQ0=sQuery(id+"F0.wireOp",EDGE,"E29.2.12");Q0=makeQuery(id+"F6.opShell","OFFSET_FACE",FACE,{"disambiguationData":[OSD([subQ0]),TDD([makeQuery(id+"F1.opExtrude","SWEPT_FACE",FACE,{"disambiguationData":[OSD([subQ0])]})])]});}
            var Q1;
            {var subQ0=sQuery(id+"F0.wireOp",EDGE,"E29.2.12");Q1=makeQuery(id+"F6.opShell","OFFSET_FACE",FACE,{"disambiguationData":[OSD([subQ0]),TDD([makeQuery(id+"F4.opChamfer","BLEND_FACE",FACE,{"disambiguationData":[OSD([subQ0]),TDD([makeQuery(id+"F1.opExtrude","CAP_EDGE",EDGE,{"disambiguationData":[OSD([subQ0])],"isStart":true})])]})])]});}
            var Q2;
            {var subQ0=sQuery(id+"F0.wireOp",EDGE,"E29.2.12");Q2=makeQuery(id+"F6.opShell","OFFSET_FACE",FACE,{"disambiguationData":[OSD([subQ0]),TDD([makeQuery(id+"F4.opChamfer","BLEND_FACE",FACE,{"disambiguationData":[OSD([subQ0]),TDD([makeQuery(id+"F1.opExtrude","CAP_EDGE",EDGE,{"disambiguationData":[OSD([subQ0])],"isStart":false})])]})])]});}
            extrude(context, id + "F8", {"entities" : qUnion([Q0, Q1, Q2]), "operationType" : NewBodyOperationType.ADD, "endBound" : BoundingType.UP_TO_NEXT, "depth" : 25 * mm, "offsetDistance" : 25 * mm});
        }
        {
            var Q0;
            {var subQ0=sQuery(id+"F0.wireOp",EDGE,"E29.3.12");Q0=makeQuery(id+"F6.opShell","OFFSET_FACE",FACE,{"disambiguationData":[OSD([subQ0]),TDD([makeQuery(id+"F1.opExtrude","SWEPT_FACE",FACE,{"disambiguationData":[OSD([subQ0])]})])]});}
            var Q1;
            {var subQ0=sQuery(id+"F0.wireOp",EDGE,"E29.3.12");Q1=makeQuery(id+"F6.opShell","OFFSET_FACE",FACE,{"disambiguationData":[OSD([subQ0]),TDD([makeQuery(id+"F4.opChamfer","BLEND_FACE",FACE,{"disambiguationData":[OSD([subQ0]),TDD([makeQuery(id+"F1.opExtrude","CAP_EDGE",EDGE,{"disambiguationData":[OSD([subQ0])],"isStart":true})])]})])]});}
            var Q2;
            {var subQ0=sQuery(id+"F0.wireOp",EDGE,"E29.3.12");Q2=makeQuery(id+"F6.opShell","OFFSET_FACE",FACE,{"disambiguationData":[OSD([subQ0]),TDD([makeQuery(id+"F4.opChamfer","BLEND_FACE",FACE,{"disambiguationData":[OSD([subQ0]),TDD([makeQuery(id+"F1.opExtrude","CAP_EDGE",EDGE,{"disambiguationData":[OSD([subQ0])],"isStart":false})])]})])]});}
            extrude(context, id + "F9", {"entities" : qUnion([Q0, Q1, Q2]), "operationType" : NewBodyOperationType.ADD, "endBound" : BoundingType.UP_TO_NEXT, "depth" : 25 * mm, "offsetDistance" : 25 * mm});
        }
        {
            var Q0;
            {var subQ0=sQuery(id+"F0.wireOp",EDGE,"E29.1.12");Q0=makeQuery(id+"F6.opShell","OFFSET_FACE",FACE,{"disambiguationData":[OSD([subQ0]),TDD([makeQuery(id+"F1.opExtrude","SWEPT_FACE",FACE,{"disambiguationData":[OSD([subQ0])]})])]});}
            var Q1;
            {var subQ0=sQuery(id+"F0.wireOp",EDGE,"E29.1.12");Q1=makeQuery(id+"F6.opShell","OFFSET_FACE",FACE,{"disambiguationData":[OSD([subQ0]),TDD([makeQuery(id+"F4.opChamfer","BLEND_FACE",FACE,{"disambiguationData":[OSD([subQ0]),TDD([makeQuery(id+"F1.opExtrude","CAP_EDGE",EDGE,{"disambiguationData":[OSD([subQ0])],"isStart":true})])]})])]});}
            var Q2;
            {var subQ0=sQuery(id+"F0.wireOp",EDGE,"E29.1.12");Q2=makeQuery(id+"F6.opShell","OFFSET_FACE",FACE,{"disambiguationData":[OSD([subQ0]),TDD([makeQuery(id+"F4.opChamfer","BLEND_FACE",FACE,{"disambiguationData":[OSD([subQ0]),TDD([makeQuery(id+"F1.opExtrude","CAP_EDGE",EDGE,{"disambiguationData":[OSD([subQ0])],"isStart":false})])]})])]});}
            extrude(context, id + "F10", {"entities" : qUnion([Q0, Q1, Q2]), "operationType" : NewBodyOperationType.ADD, "endBound" : BoundingType.UP_TO_NEXT, "depth" : 25 * mm, "offsetDistance" : 25 * mm});
        }
        {
            var Q0;
            {var subQ0=sQuery(id+"F0.wireOp",EDGE,"E24.top");Q0=makeQuery(id+"F6.opShell","OFFSET_FACE",FACE,{"disambiguationData":[OSD([subQ0]),TDD([makeQuery(id+"F1.opExtrude","SWEPT_FACE",FACE,{"disambiguationData":[OSD([subQ0])]})])]});}
            var Q1;
            {var subQ0=sQuery(id+"F0.wireOp",EDGE,"E24.top");Q1=makeQuery(id+"F6.opShell","OFFSET_FACE",FACE,{"disambiguationData":[OSD([subQ0]),TDD([makeQuery(id+"F4.opChamfer","BLEND_FACE",FACE,{"disambiguationData":[OSD([subQ0]),TDD([makeQuery(id+"F1.opExtrude","CAP_EDGE",EDGE,{"disambiguationData":[OSD([subQ0])],"isStart":true})])]})])]});}
            var Q2;
            {var subQ0=sQuery(id+"F0.wireOp",EDGE,"E24.top");Q2=makeQuery(id+"F6.opShell","OFFSET_FACE",FACE,{"disambiguationData":[OSD([subQ0]),TDD([makeQuery(id+"F4.opChamfer","BLEND_FACE",FACE,{"disambiguationData":[OSD([subQ0]),TDD([makeQuery(id+"F1.opExtrude","CAP_EDGE",EDGE,{"disambiguationData":[OSD([subQ0])],"isStart":false})])]})])]});}
            extrude(context, id + "F11", {"entities" : qUnion([Q0, Q1, Q2]), "operationType" : NewBodyOperationType.ADD, "endBound" : BoundingType.UP_TO_NEXT, "depth" : 25 * mm, "offsetDistance" : 25 * mm});
        }
        {
            var Q0;
            {var subQ0=sQuery(id+"F0.wireOp",EDGE,"E26.filletArc");var subQ1=sQuery(id+"F0.wireOp",EDGE,"E24.top");Q0=makeQuery(id+"F11.boolean.opBoolean","MERGE",FACE,{"derivedFrom":[makeQuery(id+"F11.opExtrude","SWEPT_FACE",FACE,{"disambiguationData":[OSD([subQ1,subQ0]),TDD([makeQuery(id+"F6.opShell","OFFSET_EDGE",EDGE,{"disambiguationData":[OSD([subQ1,subQ0]),TDD([makeQuery(id+"F1.opExtrude","SWEPT_EDGE",EDGE,{"disambiguationData":[OSD([subQ1,subQ0])]})])]})])]}),makeQuery(id+"F11.opExtrude","SWEPT_FACE",FACE,{"disambiguationData":[OSD([subQ1,subQ0]),TDD([makeQuery(id+"F6.opShell","OFFSET_EDGE",EDGE,{"disambiguationData":[OSD([subQ1,subQ0]),TDD([makeQuery(id+"F4.opChamfer","BLEND_EDGE",EDGE,{"blendedFrom":[makeQuery(id+"F1.opExtrude","CAP_EDGE",EDGE,{"disambiguationData":[OSD([subQ1])],"isStart":true}),makeQuery(id+"F1.opExtrude","CAP_EDGE",EDGE,{"disambiguationData":[OSD([subQ0])],"isStart":true})],"blendedInto":[]})])]})])]}),makeQuery(id+"F11.opExtrude","SWEPT_FACE",FACE,{"disambiguationData":[OSD([subQ1,subQ0]),TDD([makeQuery(id+"F6.opShell","OFFSET_EDGE",EDGE,{"disambiguationData":[OSD([subQ1,subQ0]),TDD([makeQuery(id+"F4.opChamfer","BLEND_EDGE",EDGE,{"blendedFrom":[makeQuery(id+"F1.opExtrude","CAP_EDGE",EDGE,{"disambiguationData":[OSD([subQ1])],"isStart":false}),makeQuery(id+"F1.opExtrude","CAP_EDGE",EDGE,{"disambiguationData":[OSD([subQ0])],"isStart":false})],"blendedInto":[]})])]})])]})]});}
            var Q1;
            {var subQ0=sQuery(id+"F0.wireOp",EDGE,"E29.1.12");var subQ1=sQuery(id+"F0.wireOp",EDGE,"E29.1.8");var subQ5=makeQuery(id+"F10.opExtrude","SWEPT_FACE",FACE,{"disambiguationData":[OSD([subQ1,subQ0]),TDD([makeQuery(id+"F6.opShell","OFFSET_EDGE",EDGE,{"disambiguationData":[OSD([subQ1,subQ0]),TDD([makeQuery(id+"F1.opExtrude","SWEPT_EDGE",EDGE,{"disambiguationData":[OSD([subQ1,subQ0])]})])]})])]});var subQ6=sQuery(id+"F0.wireOp",EDGE,"E0");var subQ7=makeQuery(id+"F1.opExtrude","SWEPT_FACE",FACE,{"disambiguationData":[OSD([subQ6])]});var subQ9=makeQuery(id+"F1.opExtrude","CAP_EDGE",EDGE,{"disambiguationData":[OSD([subQ6])],"isStart":true});var subQ12=sQuery(id+"F0.wireOp",EDGE,"E29.4.12");var subQ13=sQuery(id+"F0.wireOp",EDGE,"E29.4.9");var subQ14=makeQuery(id+"F7.opExtrude","SWEPT_FACE",FACE,{"disambiguationData":[OSD([subQ13,subQ12]),TDD([makeQuery(id+"F6.opShell","OFFSET_EDGE",EDGE,{"disambiguationData":[OSD([subQ13,subQ12]),TDD([makeQuery(id+"F1.opExtrude","SWEPT_EDGE",EDGE,{"disambiguationData":[OSD([subQ13,subQ12])]})])]})])]});Q1=makeQuery(id+"F11.boolean.opBoolean","SPLIT",EDGE,{"disambiguationData":[TD([subQ5])],"derivedFrom":makeQuery(id+"F10.boolean.opBoolean","SPLIT",EDGE,{"disambiguationData":[TD([subQ14])],"derivedFrom":makeQuery(id+"F8.boolean.opBoolean","SPLIT",EDGE,{"disambiguationData":[TD([subQ14])],"derivedFrom":makeQuery(id+"F6.opShell","OFFSET_EDGE",EDGE,{"disambiguationData":[OSD([subQ6]),TDD([makeQuery(id+"F5.opChamfer","BLEND_EDGE",EDGE,{"blendedFrom":[subQ9,subQ7],"blendedInto":[subQ7]})])]})})})});}
            sweep(context, id + "F12", {"operationType" : NewBodyOperationType.ADD, "profiles" : qUnion([Q0]), "path" : qUnion([Q1])});
        }
        {
            var Q0;
            {var subQ0=sQuery(id+"F0.wireOp",EDGE,"E29.1.12");var subQ1=sQuery(id+"F0.wireOp",EDGE,"E29.1.9");Q0=makeQuery(id+"F10.boolean.opBoolean","MERGE",FACE,{"derivedFrom":[makeQuery(id+"F10.opExtrude","SWEPT_FACE",FACE,{"disambiguationData":[OSD([subQ1,subQ0]),TDD([makeQuery(id+"F6.opShell","OFFSET_EDGE",EDGE,{"disambiguationData":[OSD([subQ1,subQ0]),TDD([makeQuery(id+"F1.opExtrude","SWEPT_EDGE",EDGE,{"disambiguationData":[OSD([subQ1,subQ0])]})])]})])]}),makeQuery(id+"F10.opExtrude","SWEPT_FACE",FACE,{"disambiguationData":[OSD([subQ1,subQ0]),TDD([makeQuery(id+"F6.opShell","OFFSET_EDGE",EDGE,{"disambiguationData":[OSD([subQ1,subQ0]),TDD([makeQuery(id+"F4.opChamfer","BLEND_EDGE",EDGE,{"blendedFrom":[makeQuery(id+"F1.opExtrude","CAP_EDGE",EDGE,{"disambiguationData":[OSD([subQ1])],"isStart":true}),makeQuery(id+"F1.opExtrude","CAP_EDGE",EDGE,{"disambiguationData":[OSD([subQ0])],"isStart":true})],"blendedInto":[]})])]})])]}),makeQuery(id+"F10.opExtrude","SWEPT_FACE",FACE,{"disambiguationData":[OSD([subQ1,subQ0]),TDD([makeQuery(id+"F6.opShell","OFFSET_EDGE",EDGE,{"disambiguationData":[OSD([subQ1,subQ0]),TDD([makeQuery(id+"F4.opChamfer","BLEND_EDGE",EDGE,{"blendedFrom":[makeQuery(id+"F1.opExtrude","CAP_EDGE",EDGE,{"disambiguationData":[OSD([subQ1])],"isStart":false}),makeQuery(id+"F1.opExtrude","CAP_EDGE",EDGE,{"disambiguationData":[OSD([subQ0])],"isStart":false})],"blendedInto":[]})])]})])]})]});}
            var Q1;
            {var subQ0=sQuery(id+"F0.wireOp",EDGE,"E29.2.12");var subQ1=sQuery(id+"F0.wireOp",EDGE,"E29.2.8");var subQ2=makeQuery(id+"F8.opExtrude","SWEPT_FACE",FACE,{"disambiguationData":[OSD([subQ1,subQ0]),TDD([makeQuery(id+"F6.opShell","OFFSET_EDGE",EDGE,{"disambiguationData":[OSD([subQ1,subQ0]),TDD([makeQuery(id+"F1.opExtrude","SWEPT_EDGE",EDGE,{"disambiguationData":[OSD([subQ1,subQ0])]})])]})])]});var subQ3=sQuery(id+"F0.wireOp",EDGE,"E0");var subQ4=makeQuery(id+"F1.opExtrude","SWEPT_FACE",FACE,{"disambiguationData":[OSD([subQ3])]});var subQ8=makeQuery(id+"F1.opExtrude","CAP_EDGE",EDGE,{"disambiguationData":[OSD([subQ3])],"isStart":true});var subQ12=sQuery(id+"F0.wireOp",EDGE,"E29.4.12");var subQ13=sQuery(id+"F0.wireOp",EDGE,"E29.4.9");Q1=makeQuery(id+"F10.boolean.opBoolean","SPLIT",EDGE,{"disambiguationData":[TD([subQ2])],"derivedFrom":makeQuery(id+"F8.boolean.opBoolean","SPLIT",EDGE,{"disambiguationData":[TD([makeQuery(id+"F7.opExtrude","SWEPT_FACE",FACE,{"disambiguationData":[OSD([subQ13,subQ12]),TDD([makeQuery(id+"F6.opShell","OFFSET_EDGE",EDGE,{"disambiguationData":[OSD([subQ13,subQ12]),TDD([makeQuery(id+"F1.opExtrude","SWEPT_EDGE",EDGE,{"disambiguationData":[OSD([subQ13,subQ12])]})])]})])]})])],"derivedFrom":makeQuery(id+"F6.opShell","OFFSET_EDGE",EDGE,{"disambiguationData":[OSD([subQ3]),TDD([makeQuery(id+"F5.opChamfer","BLEND_EDGE",EDGE,{"blendedFrom":[subQ8,subQ4],"blendedInto":[subQ4]})])]})})});}
            sweep(context, id + "F13", {"operationType" : NewBodyOperationType.ADD, "profiles" : qUnion([Q0]), "path" : qUnion([Q1])});
        }
        {
            var Q0;
            {var subQ0=sQuery(id+"F0.wireOp",EDGE,"E29.2.12");var subQ1=sQuery(id+"F0.wireOp",EDGE,"E29.2.9");Q0=makeQuery(id+"F8.boolean.opBoolean","MERGE",FACE,{"derivedFrom":[makeQuery(id+"F8.opExtrude","SWEPT_FACE",FACE,{"disambiguationData":[OSD([subQ1,subQ0]),TDD([makeQuery(id+"F6.opShell","OFFSET_EDGE",EDGE,{"disambiguationData":[OSD([subQ1,subQ0]),TDD([makeQuery(id+"F1.opExtrude","SWEPT_EDGE",EDGE,{"disambiguationData":[OSD([subQ1,subQ0])]})])]})])]}),makeQuery(id+"F8.opExtrude","SWEPT_FACE",FACE,{"disambiguationData":[OSD([subQ1,subQ0]),TDD([makeQuery(id+"F6.opShell","OFFSET_EDGE",EDGE,{"disambiguationData":[OSD([subQ1,subQ0]),TDD([makeQuery(id+"F4.opChamfer","BLEND_EDGE",EDGE,{"blendedFrom":[makeQuery(id+"F1.opExtrude","CAP_EDGE",EDGE,{"disambiguationData":[OSD([subQ1])],"isStart":true}),makeQuery(id+"F1.opExtrude","CAP_EDGE",EDGE,{"disambiguationData":[OSD([subQ0])],"isStart":true})],"blendedInto":[]})])]})])]}),makeQuery(id+"F8.opExtrude","SWEPT_FACE",FACE,{"disambiguationData":[OSD([subQ1,subQ0]),TDD([makeQuery(id+"F6.opShell","OFFSET_EDGE",EDGE,{"disambiguationData":[OSD([subQ1,subQ0]),TDD([makeQuery(id+"F4.opChamfer","BLEND_EDGE",EDGE,{"blendedFrom":[makeQuery(id+"F1.opExtrude","CAP_EDGE",EDGE,{"disambiguationData":[OSD([subQ1])],"isStart":false}),makeQuery(id+"F1.opExtrude","CAP_EDGE",EDGE,{"disambiguationData":[OSD([subQ0])],"isStart":false})],"blendedInto":[]})])]})])]})]});}
            var Q1;
            {var subQ0=sQuery(id+"F0.wireOp",EDGE,"E29.2.12");var subQ1=sQuery(id+"F0.wireOp",EDGE,"E29.2.9");var subQ2=makeQuery(id+"F8.opExtrude","SWEPT_FACE",FACE,{"disambiguationData":[OSD([subQ1,subQ0]),TDD([makeQuery(id+"F6.opShell","OFFSET_EDGE",EDGE,{"disambiguationData":[OSD([subQ1,subQ0]),TDD([makeQuery(id+"F1.opExtrude","SWEPT_EDGE",EDGE,{"disambiguationData":[OSD([subQ1,subQ0])]})])]})])]});var subQ3=sQuery(id+"F0.wireOp",EDGE,"E0");var subQ4=makeQuery(id+"F1.opExtrude","CAP_EDGE",EDGE,{"disambiguationData":[OSD([subQ3])],"isStart":true});var subQ7=makeQuery(id+"F1.opExtrude","SWEPT_FACE",FACE,{"disambiguationData":[OSD([subQ3])]});var subQ12=sQuery(id+"F0.wireOp",EDGE,"E29.4.12");var subQ13=sQuery(id+"F0.wireOp",EDGE,"E29.4.8");Q1=makeQuery(id+"F9.boolean.opBoolean","SPLIT",EDGE,{"disambiguationData":[TD([subQ2])],"derivedFrom":makeQuery(id+"F8.boolean.opBoolean","SPLIT",EDGE,{"disambiguationData":[TD([makeQuery(id+"F7.opExtrude","SWEPT_FACE",FACE,{"disambiguationData":[OSD([subQ13,subQ12]),TDD([makeQuery(id+"F6.opShell","OFFSET_EDGE",EDGE,{"disambiguationData":[OSD([subQ13,subQ12]),TDD([makeQuery(id+"F1.opExtrude","SWEPT_EDGE",EDGE,{"disambiguationData":[OSD([subQ13,subQ12])]})])]})])]})])],"derivedFrom":makeQuery(id+"F6.opShell","OFFSET_EDGE",EDGE,{"disambiguationData":[OSD([subQ3]),TDD([makeQuery(id+"F5.opChamfer","BLEND_EDGE",EDGE,{"blendedFrom":[subQ4,subQ7],"blendedInto":[subQ7]})])]})})});}
            sweep(context, id + "F14", {"operationType" : NewBodyOperationType.ADD, "profiles" : qUnion([Q0]), "path" : qUnion([Q1])});
        }
        {
            var Q0;
            {var subQ0=sQuery(id+"F0.wireOp",EDGE,"E29.4.12");var subQ1=sQuery(id+"F0.wireOp",EDGE,"E29.4.9");Q0=makeQuery(id+"F7.boolean.opBoolean","MERGE",FACE,{"derivedFrom":[makeQuery(id+"F7.opExtrude","SWEPT_FACE",FACE,{"disambiguationData":[OSD([subQ1,subQ0]),TDD([makeQuery(id+"F6.opShell","OFFSET_EDGE",EDGE,{"disambiguationData":[OSD([subQ1,subQ0]),TDD([makeQuery(id+"F1.opExtrude","SWEPT_EDGE",EDGE,{"disambiguationData":[OSD([subQ1,subQ0])]})])]})])]}),makeQuery(id+"F7.opExtrude","SWEPT_FACE",FACE,{"disambiguationData":[OSD([subQ1,subQ0]),TDD([makeQuery(id+"F6.opShell","OFFSET_EDGE",EDGE,{"disambiguationData":[OSD([subQ1,subQ0]),TDD([makeQuery(id+"F4.opChamfer","BLEND_EDGE",EDGE,{"blendedFrom":[makeQuery(id+"F1.opExtrude","CAP_EDGE",EDGE,{"disambiguationData":[OSD([subQ1])],"isStart":true}),makeQuery(id+"F1.opExtrude","CAP_EDGE",EDGE,{"disambiguationData":[OSD([subQ0])],"isStart":true})],"blendedInto":[]})])]})])]}),makeQuery(id+"F7.opExtrude","SWEPT_FACE",FACE,{"disambiguationData":[OSD([subQ1,subQ0]),TDD([makeQuery(id+"F6.opShell","OFFSET_EDGE",EDGE,{"disambiguationData":[OSD([subQ1,subQ0]),TDD([makeQuery(id+"F4.opChamfer","BLEND_EDGE",EDGE,{"blendedFrom":[makeQuery(id+"F1.opExtrude","CAP_EDGE",EDGE,{"disambiguationData":[OSD([subQ1])],"isStart":false}),makeQuery(id+"F1.opExtrude","CAP_EDGE",EDGE,{"disambiguationData":[OSD([subQ0])],"isStart":false})],"blendedInto":[]})])]})])]})]});}
            var Q1;
            {var subQ0=sQuery(id+"F0.wireOp",EDGE,"E29.4.12");var subQ1=sQuery(id+"F0.wireOp",EDGE,"E29.4.9");var subQ2=makeQuery(id+"F7.opExtrude","SWEPT_FACE",FACE,{"disambiguationData":[OSD([subQ1,subQ0]),TDD([makeQuery(id+"F6.opShell","OFFSET_EDGE",EDGE,{"disambiguationData":[OSD([subQ1,subQ0]),TDD([makeQuery(id+"F1.opExtrude","SWEPT_EDGE",EDGE,{"disambiguationData":[OSD([subQ1,subQ0])]})])]})])]});var subQ5=sQuery(id+"F0.wireOp",EDGE,"E0");var subQ6=makeQuery(id+"F1.opExtrude","SWEPT_FACE",FACE,{"disambiguationData":[OSD([subQ5])]});var subQ9=makeQuery(id+"F1.opExtrude","CAP_EDGE",EDGE,{"disambiguationData":[OSD([subQ5])],"isStart":true});Q1=makeQuery(id+"F11.boolean.opBoolean","SPLIT",EDGE,{"disambiguationData":[TD([subQ2])],"derivedFrom":makeQuery(id+"F10.boolean.opBoolean","SPLIT",EDGE,{"disambiguationData":[TD([subQ2])],"derivedFrom":makeQuery(id+"F8.boolean.opBoolean","SPLIT",EDGE,{"disambiguationData":[TD([subQ2])],"derivedFrom":makeQuery(id+"F6.opShell","OFFSET_EDGE",EDGE,{"disambiguationData":[OSD([subQ5]),TDD([makeQuery(id+"F5.opChamfer","BLEND_EDGE",EDGE,{"blendedFrom":[subQ9,subQ6],"blendedInto":[subQ6]})])]})})})});}
            sweep(context, id + "F15", {"operationType" : NewBodyOperationType.ADD, "profiles" : qUnion([Q0]), "path" : qUnion([Q1])});
        }
        {
            var Q0;
            {var subQ0=sQuery(id+"F0.wireOp",EDGE,"E29.4.12");var subQ1=sQuery(id+"F0.wireOp",EDGE,"E29.4.8");Q0=makeQuery(id+"F7.boolean.opBoolean","MERGE",FACE,{"derivedFrom":[makeQuery(id+"F7.opExtrude","SWEPT_FACE",FACE,{"disambiguationData":[OSD([subQ1,subQ0]),TDD([makeQuery(id+"F6.opShell","OFFSET_EDGE",EDGE,{"disambiguationData":[OSD([subQ1,subQ0]),TDD([makeQuery(id+"F1.opExtrude","SWEPT_EDGE",EDGE,{"disambiguationData":[OSD([subQ1,subQ0])]})])]})])]}),makeQuery(id+"F7.opExtrude","SWEPT_FACE",FACE,{"disambiguationData":[OSD([subQ1,subQ0]),TDD([makeQuery(id+"F6.opShell","OFFSET_EDGE",EDGE,{"disambiguationData":[OSD([subQ1,subQ0]),TDD([makeQuery(id+"F4.opChamfer","BLEND_EDGE",EDGE,{"blendedFrom":[makeQuery(id+"F1.opExtrude","CAP_EDGE",EDGE,{"disambiguationData":[OSD([subQ1])],"isStart":true}),makeQuery(id+"F1.opExtrude","CAP_EDGE",EDGE,{"disambiguationData":[OSD([subQ0])],"isStart":true})],"blendedInto":[]})])]})])]}),makeQuery(id+"F7.opExtrude","SWEPT_FACE",FACE,{"disambiguationData":[OSD([subQ1,subQ0]),TDD([makeQuery(id+"F6.opShell","OFFSET_EDGE",EDGE,{"disambiguationData":[OSD([subQ1,subQ0]),TDD([makeQuery(id+"F4.opChamfer","BLEND_EDGE",EDGE,{"blendedFrom":[makeQuery(id+"F1.opExtrude","CAP_EDGE",EDGE,{"disambiguationData":[OSD([subQ1])],"isStart":false}),makeQuery(id+"F1.opExtrude","CAP_EDGE",EDGE,{"disambiguationData":[OSD([subQ0])],"isStart":false})],"blendedInto":[]})])]})])]})]});}
            var Q1;
            {var subQ0=sQuery(id+"F0.wireOp",EDGE,"E29.4.12");var subQ1=sQuery(id+"F0.wireOp",EDGE,"E29.4.8");var subQ3=makeQuery(id+"F7.opExtrude","SWEPT_FACE",FACE,{"disambiguationData":[OSD([subQ1,subQ0]),TDD([makeQuery(id+"F6.opShell","OFFSET_EDGE",EDGE,{"disambiguationData":[OSD([subQ1,subQ0]),TDD([makeQuery(id+"F1.opExtrude","SWEPT_EDGE",EDGE,{"disambiguationData":[OSD([subQ1,subQ0])]})])]})])]});var subQ4=sQuery(id+"F0.wireOp",EDGE,"E0");var subQ5=makeQuery(id+"F1.opExtrude","SWEPT_FACE",FACE,{"disambiguationData":[OSD([subQ4])]});var subQ7=makeQuery(id+"F1.opExtrude","CAP_EDGE",EDGE,{"disambiguationData":[OSD([subQ4])],"isStart":true});Q1=makeQuery(id+"F9.boolean.opBoolean","SPLIT",EDGE,{"disambiguationData":[TD([subQ3])],"derivedFrom":makeQuery(id+"F8.boolean.opBoolean","SPLIT",EDGE,{"disambiguationData":[TD([subQ3])],"derivedFrom":makeQuery(id+"F6.opShell","OFFSET_EDGE",EDGE,{"disambiguationData":[OSD([subQ4]),TDD([makeQuery(id+"F5.opChamfer","BLEND_EDGE",EDGE,{"blendedFrom":[subQ7,subQ5],"blendedInto":[subQ5]})])]})})});}
            sweep(context, id + "F16", {"operationType" : NewBodyOperationType.ADD, "profiles" : qUnion([Q0]), "path" : qUnion([Q1])});
        }
    });
